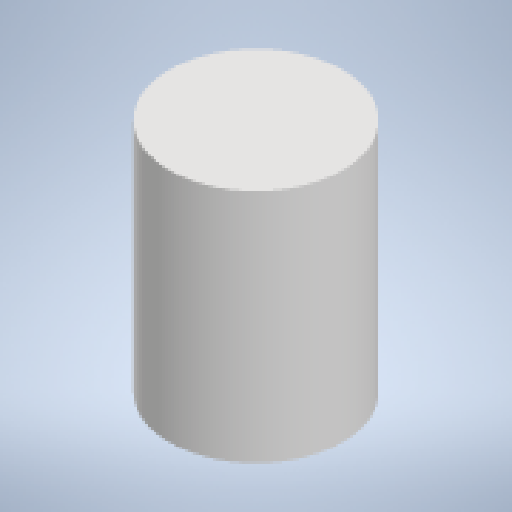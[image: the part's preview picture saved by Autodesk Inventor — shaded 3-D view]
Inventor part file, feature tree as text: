
AUTODESK INVENTOR PART (.ipt)
format: ipt  version: 2025 (Build 290162010, 162A)  size: 119,808 bytes
history: native  units: mm
features: other x1, extrude x1, sketch x1
ambient origin geometry x8: Origin, YZ Plane, XZ Plane, XY Plane, X Axis, Y Axis, Z Axis, Center Point
bodies: Body1 (feature_tree)
feature tree (3):
  other  "body 1"
  extrude  "Extrusion1"  Depth=2170.0mm TaperAngle=0.0deg
  sketch  "Sketch1"  dims[d0=1600.0mm d1=2170.0mm d2=0.0mm]
